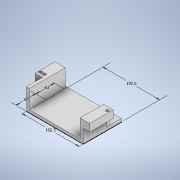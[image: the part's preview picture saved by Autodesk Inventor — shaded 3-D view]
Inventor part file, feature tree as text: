
AUTODESK INVENTOR PART (.ipt)
format: ipt  version: 2020 (Build 240168000, 168)  size: 159,744 bytes
history: native  units: mm
features: sketch x5, extrude x4, projected_geometry x2, other x1, hole x1
ambient origin geometry x8: Origin, YZ Plane, XZ Plane, XY Plane, X Axis, Y Axis, Z Axis, Center Point
bodies: Body1 (feature_tree)
feature tree (13):
  other  "솔리드1"
  sketch  "스케치1"
  extrude  "돌출1"  Depth=192.5mm
  extrude  "돌출2"  Depth=67.0mm
  extrude  "돌출3"  Depth=192.5mm
  extrude  "돌출4"  Depth=63.0mm
  hole  "구멍1"  [1 undecoded]
  sketch  "스케치2"
  sketch  "스케치3"
  projected_geometry  "투영된 루프1"
  sketch  "스케치5"
  projected_geometry  "투영된 루프2"
  sketch  "스케치6"
note: 1 required parameter value undecoded (feature->parameter linkage not recoverable at this tier; creation-order binding heuristic only, values carry confidence <= 0.55)
